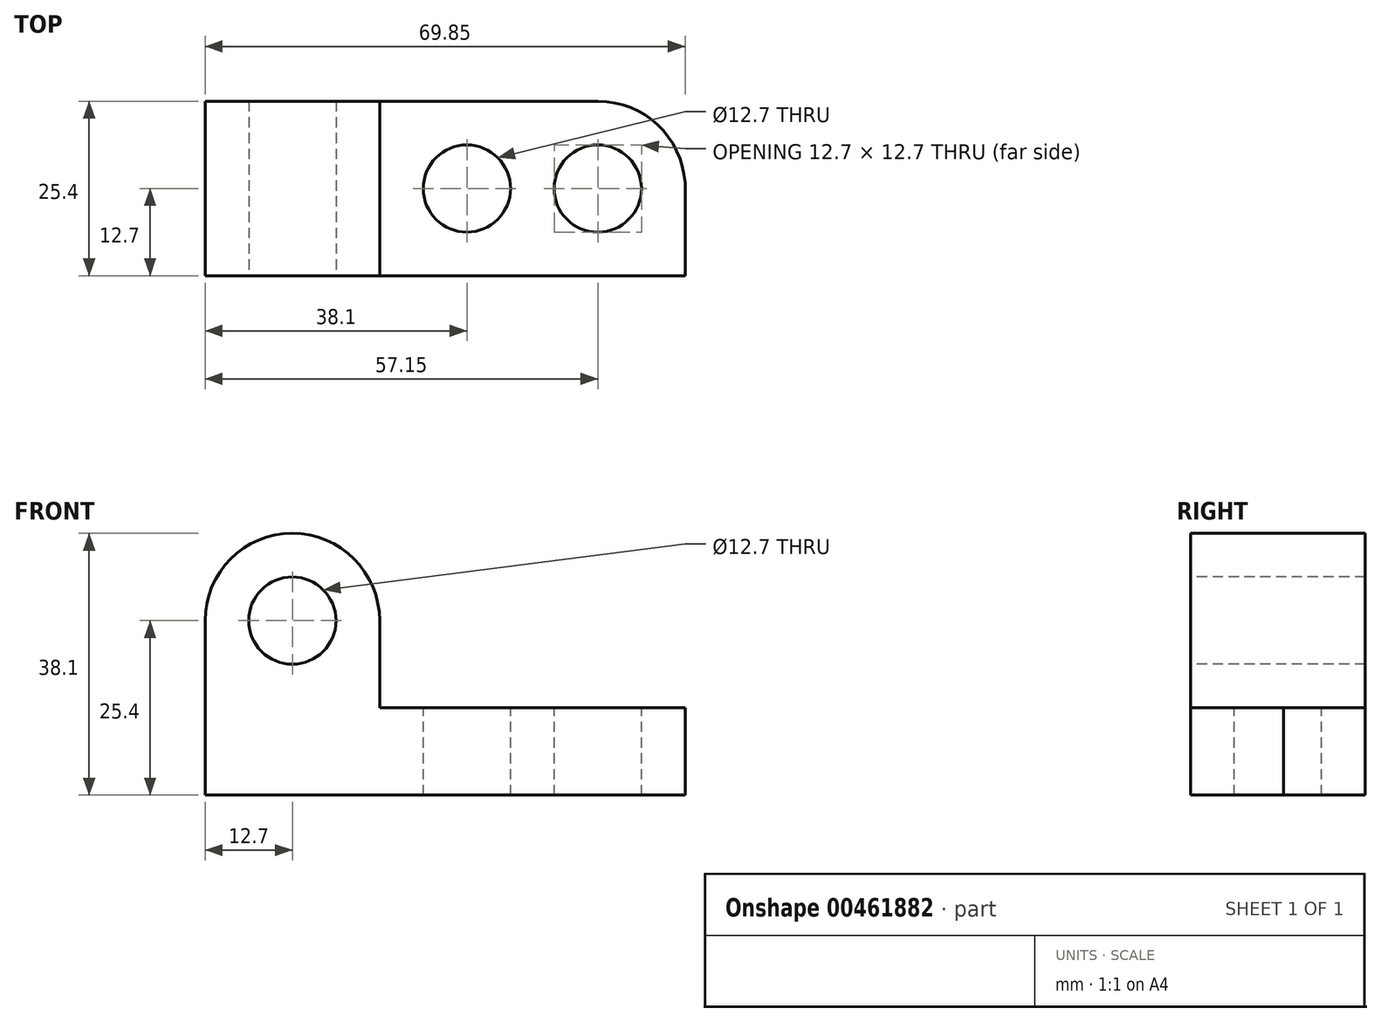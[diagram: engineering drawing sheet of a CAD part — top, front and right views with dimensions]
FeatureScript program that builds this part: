
annotation { "Feature Type Name" : "Feature", "Feature Type Description" : "" }
export const myFeature = defineFeature(function(context is Context, id is Id, definition is map)
    precondition{}
    {
        {
            var Q0;
            Q0=qCreatedBy(makeId("Front.planeOp"),FACE);
            var sketch = newSketch(context, id + "F0", { "sketchPlane" : qUnion([Q0])});
            skLineSegment(sketch, "E0", {"start": v(0, 0) * mm, "end": v(69.85, 0) * mm});
            skLineSegment(sketch, "E1", {"start": v(69.85, 0) * mm, "end": v(69.85, 12.7) * mm});
            skLineSegment(sketch, "E2", {"start": v(69.85, 12.7) * mm, "end": v(25.4, 12.7) * mm});
            skLineSegment(sketch, "E3", {"start": v(25.4, 12.7) * mm, "end": v(25.4, 38.1) * mm});
            skLineSegment(sketch, "E4", {"start": v(25.4, 38.1) * mm, "end": v(0, 38.1) * mm});
            skLineSegment(sketch, "E5", {"start": v(0, 38.1) * mm, "end": v(0, 0) * mm});
            skSolve(sketch);
        }
        {
            var Q0;
            Q0=makeQuery(id+"F0.imprint","IMPRINT",FACE,{"disambiguationData":[TD([[makeQuery(id+"F0.imprint","IMPRINT",EDGE,{"derivedFrom":sQuery(id+"F0.wireOp",EDGE,"E0")}),1.0]])]});
            extrude(context, id + "F1", {"entities" : qUnion([Q0]), "depth" : 25.4 * mm});
        }
        {
            var Q0;
            Q0=makeQuery(id+"F1.opExtrude","CAP_FACE",FACE,{"disambiguationData":[OSD([sQuery(id+"F0.wireOp",EDGE,"E0"),sQuery(id+"F0.wireOp",EDGE,"E1"),sQuery(id+"F0.wireOp",EDGE,"E2"),sQuery(id+"F0.wireOp",EDGE,"E3"),sQuery(id+"F0.wireOp",EDGE,"E4"),sQuery(id+"F0.wireOp",EDGE,"E5")])],"isStart":false});
            var sketch = newSketch(context, id + "F2", { "sketchPlane" : qUnion([Q0])});
            skCircle(sketch, "E6", {"center": v(12.7, 25.4) * mm, "radius": 6.35 * mm});
            skArc(sketch, "E7", {"start": v(25.4, 25.4) * mm, "mid": v(12.7, 38.1) * mm, "end": v(0, 25.4) * mm});
            skPoint(sketch, "E7.endSnap0", {"position": v(25.4, 25.4) * mm});
            skSolve(sketch);
        }
        {
            var Q0;
            Q0=makeQuery(id+"F2.imprint","IMPRINT",FACE,{"disambiguationData":[TD([[makeQuery(id+"F2.imprint","IMPRINT",EDGE,{"derivedFrom":sQuery(id+"F2.wireOp",EDGE,"E6")}),1.0]])]});
            var Q1;
            {var subQ0=sQuery(id+"F2.wireOp",EDGE,"E7");var subQ1=makeQuery(id+"F1.opExtrude","CAP_EDGE",EDGE,{"disambiguationData":[OSD([sQuery(id+"F0.wireOp",EDGE,"E3")])],"isStart":false});var subQ2=makeQuery(id+"F2.imprint","INTERSECT",VERTEX,{"derivedFrom":[subQ1,subQ0]});Q1=makeQuery(id+"F2.imprint","IMPRINT",FACE,{"disambiguationData":[TD([[makeQuery(id+"F2.imprint","IMPRINT",EDGE,{"disambiguationData":[TD([[subQ2,-1.0]])],"derivedFrom":subQ0}),-1.0]])]});}
            var Q2;
            {var subQ0=sQuery(id+"F2.wireOp",EDGE,"E7");var subQ1=makeQuery(id+"F1.opExtrude","CAP_EDGE",EDGE,{"disambiguationData":[OSD([sQuery(id+"F0.wireOp",EDGE,"E5")])],"isStart":false});var subQ2=makeQuery(id+"F2.imprint","INTERSECT",VERTEX,{"derivedFrom":[subQ1,subQ0]});Q2=makeQuery(id+"F2.imprint","IMPRINT",FACE,{"disambiguationData":[TD([[makeQuery(id+"F2.imprint","IMPRINT",EDGE,{"disambiguationData":[TD([[subQ2,1.0]])],"derivedFrom":subQ0}),-1.0]])]});}
            extrude(context, id + "F3", {"entities" : qUnion([Q0, Q1, Q2]), "operationType" : NewBodyOperationType.REMOVE, "oppositeDirection" : true, "depth" : 25.4 * mm});
        }
        {
            var Q0;
            Q0=makeQuery(id+"F1.opExtrude","SWEPT_FACE",FACE,{"disambiguationData":[OSD([sQuery(id+"F0.wireOp",EDGE,"E2")])]});
            var sketch = newSketch(context, id + "F4", { "sketchPlane" : qUnion([Q0])});
            skCircle(sketch, "E8", {"center": v(38.1, -12.7) * mm, "radius": 6.35 * mm});
            skCircle(sketch, "E9", {"center": v(57.15, -12.7) * mm, "radius": 6.35 * mm});
            skArc(sketch, "E10", {"start": v(57.15, -25.4) * mm, "mid": v(69.88, -12.7) * mm, "end": v(57.15, 0) * mm});
            skLineSegment(sketch, "E11", {"start": v(38.1, -19.05) * mm, "end": v(57.18, -19.05) * mm});
            skLineSegment(sketch, "E12", {"start": v(57.18, -6.35) * mm, "end": v(38.1, -6.27) * mm});
            skSolve(sketch);
        }
        {
            var Q0;
            Q0=makeQuery(id+"F4.imprint","IMPRINT",FACE,{"disambiguationData":[TD([[makeQuery(id+"F4.imprint","IMPRINT",EDGE,{"derivedFrom":sQuery(id+"F4.wireOp",EDGE,"E8")}),1.0]])]});
            var Q1;
            {var subQ0=sQuery(id+"F4.wireOp",EDGE,"E9");var subQ1=makeQuery(id+"F4.imprint","IMPRINT",VERTEX,{"disambiguationData":[OD(0.0)],"derivedFrom":subQ0});Q1=makeQuery(id+"F4.imprint","IMPRINT",FACE,{"disambiguationData":[TD([[makeQuery(id+"F4.imprint","IMPRINT",EDGE,{"disambiguationData":[TD([[subQ1,1.0]])],"derivedFrom":subQ0}),1.0]])]});}
            var Q2;
            {var subQ0=sQuery(id+"F4.wireOp",EDGE,"E10");var subQ1=sQuery(id+"F0.wireOp",EDGE,"E2");var subQ4=makeQuery(id+"F1.opExtrude","SWEPT_EDGE",EDGE,{"disambiguationData":[OSD([sQuery(id+"F0.wireOp",EDGE,"E1"),subQ1])]});var subQ5=makeQuery(id+"F4.imprint","INTERSECT",VERTEX,{"disambiguationData":[OD(0.0)],"derivedFrom":[subQ4,subQ0]});Q2=makeQuery(id+"F4.imprint","IMPRINT",FACE,{"disambiguationData":[TD([[makeQuery(id+"F4.imprint","IMPRINT",EDGE,{"disambiguationData":[TD([[subQ5,1.0]])],"derivedFrom":subQ0}),-1.0]])]});}
            var Q3;
            {var subQ0=sQuery(id+"F4.wireOp",EDGE,"E10");var subQ1=sQuery(id+"F0.wireOp",EDGE,"E2");var subQ2=makeQuery(id+"F1.opExtrude","CAP_EDGE",EDGE,{"disambiguationData":[OSD([subQ1])],"isStart":true});var subQ3=makeQuery(id+"F4.imprint","INTERSECT",VERTEX,{"derivedFrom":[subQ2,subQ0]});Q3=makeQuery(id+"F4.imprint","IMPRINT",FACE,{"disambiguationData":[TD([[makeQuery(id+"F4.imprint","IMPRINT",EDGE,{"disambiguationData":[TD([[subQ3,1.0]])],"derivedFrom":subQ0}),-1.0]])]});}
            extrude(context, id + "F5", {"entities" : qUnion([Q0, Q1, Q2, Q3]), "operationType" : NewBodyOperationType.REMOVE, "oppositeDirection" : true, "depth" : 12.7 * mm});
        }
        {
            var Q0;
            Q0=makeQuery(id+"F1.opExtrude","SWEPT_FACE",FACE,{"disambiguationData":[OSD([sQuery(id+"F0.wireOp",EDGE,"E2")])]});
            var sketch = newSketch(context, id + "F6", { "sketchPlane" : qUnion([Q0])});
            skLineSegment(sketch, "E13", {"start": v(56.92, -6.35) * mm, "end": v(37.87, -6.35) * mm});
            skLineSegment(sketch, "E14", {"start": v(37.76, -19.04) * mm, "end": v(57.15, -19.05) * mm});
            skSolve(sketch);
        }
        {
            var Q0;
            {var subQ0=sQuery(id+"F6.wireOp",EDGE,"E13");var subQ1=makeQuery(id+"F5.boolean.opBoolean","COPY",EDGE,{"derivedFrom":makeQuery(id+"F5.opExtrude","CAP_EDGE",EDGE,{"disambiguationData":[OSD([sQuery(id+"F4.wireOp",EDGE,"E9")])],"isStart":true})});var subQ2=makeQuery(id+"F6.imprint","INTERSECT",VERTEX,{"derivedFrom":[subQ1,subQ0]});Q0=makeQuery(id+"F6.imprint","IMPRINT",FACE,{"disambiguationData":[TD([[makeQuery(id+"F6.imprint","IMPRINT",EDGE,{"disambiguationData":[TD([[subQ2,-1.0]])],"derivedFrom":subQ0}),1.0]])]});}
            extrude(context, id + "F7", {"entities" : qUnion([Q0]), "operationType" : NewBodyOperationType.REMOVE, "oppositeDirection" : true, "depth" : 12.7 * mm});
        }
    });
